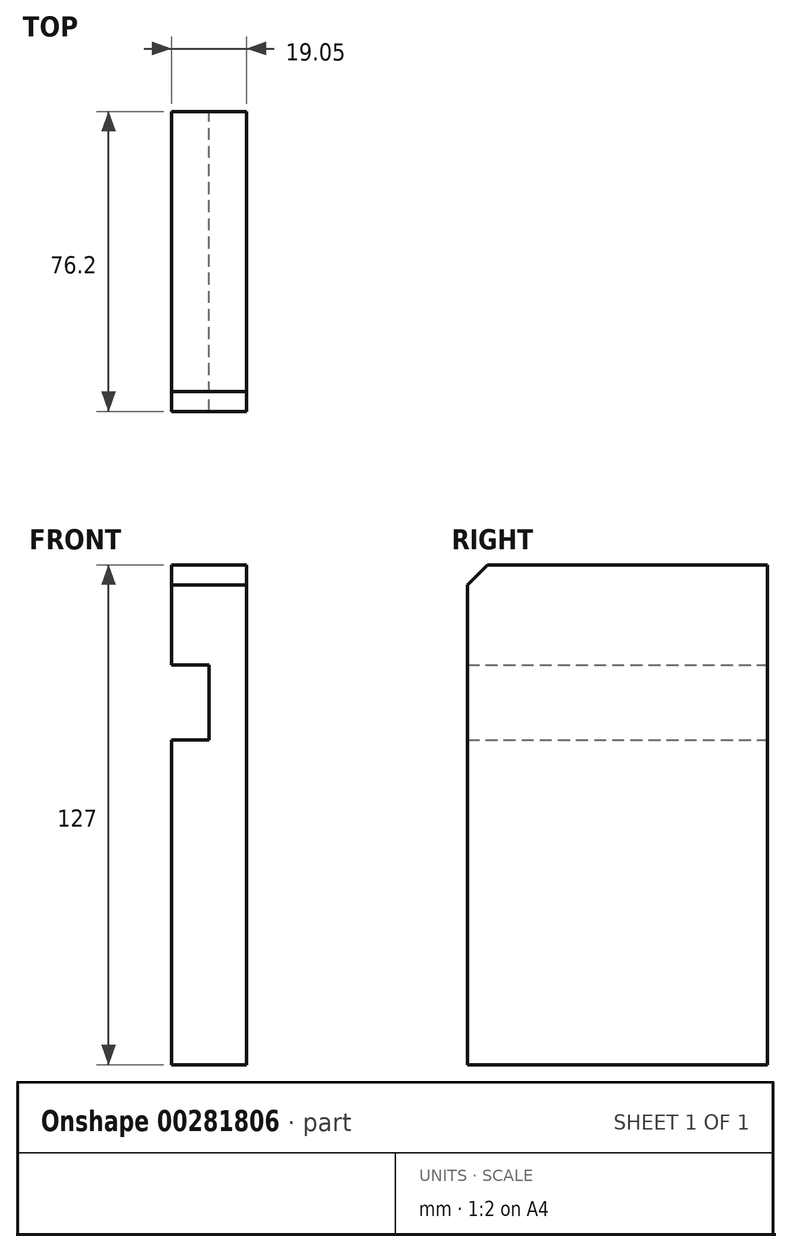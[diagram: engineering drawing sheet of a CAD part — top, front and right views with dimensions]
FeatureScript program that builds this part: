
annotation { "Feature Type Name" : "Feature", "Feature Type Description" : "" }
export const myFeature = defineFeature(function(context is Context, id is Id, definition is map)
    precondition{}
    {
        {
            var Q0;
            Q0=qCreatedBy(makeId("Front.planeOp"),FACE);
            var sketch = newSketch(context, id + "F0", { "sketchPlane" : qUnion([Q0])});
            skLineSegment(sketch, "E0", {"start": v(0, 0) * mm, "end": v(0, 127) * mm});
            skLineSegment(sketch, "E1", {"start": v(0, 127) * mm, "end": v(-19.05, 127) * mm});
            skLineSegment(sketch, "E2", {"start": v(-19.05, 127) * mm, "end": v(-19.05, 101.6) * mm});
            skLineSegment(sketch, "E3", {"start": v(-19.05, 101.6) * mm, "end": v(-9.52, 101.6) * mm});
            skLineSegment(sketch, "E4", {"start": v(-9.52, 101.6) * mm, "end": v(-9.52, 82.55) * mm});
            skLineSegment(sketch, "E5", {"start": v(-9.52, 82.55) * mm, "end": v(-19.05, 82.55) * mm});
            skLineSegment(sketch, "E6", {"start": v(-19.05, 82.55) * mm, "end": v(-19.05, 0) * mm});
            skLineSegment(sketch, "E7", {"start": v(-19.05, 0) * mm, "end": v(0, 0) * mm});
            skSolve(sketch);
        }
        {
            var Q0;
            Q0=makeQuery(id+"F0.imprint","IMPRINT",FACE,{"disambiguationData":[TD([[makeQuery(id+"F0.imprint","IMPRINT",EDGE,{"derivedFrom":sQuery(id+"F0.wireOp",EDGE,"E0")}),1.0]])]});
            extrude(context, id + "F1", {"entities" : qUnion([Q0]), "depth" : 76.2 * mm});
        }
        {
            var Q0;
            Q0=makeQuery(id+"F1.opExtrude","CAP_EDGE",EDGE,{"disambiguationData":[OSD([sQuery(id+"F0.wireOp",EDGE,"E1")])],"isStart":false});
            chamfer(context, id + "F2", {"entities" : qUnion([Q0]), "width" : 5.08 * mm, "tangentPropagation" : true});
        }
    });
